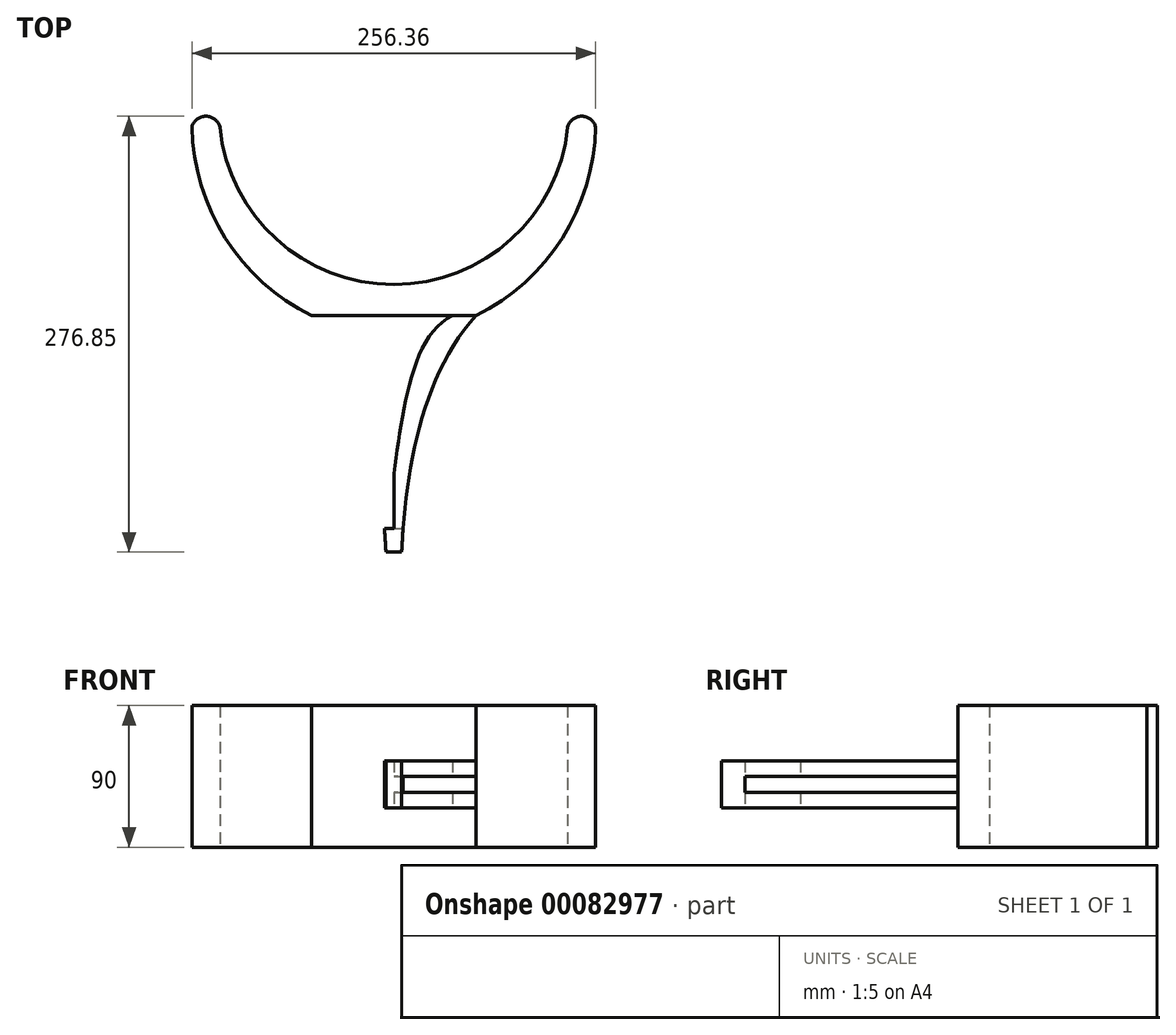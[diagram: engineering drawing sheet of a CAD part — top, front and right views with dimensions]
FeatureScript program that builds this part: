
annotation { "Feature Type Name" : "Feature", "Feature Type Description" : "" }
export const myFeature = defineFeature(function(context is Context, id is Id, definition is map)
    precondition{}
    {
        {
            var Q0;
            Q0=qCreatedBy(makeId("Top.planeOp"),FACE);
            var sketch = newSketch(context, id + "F0", { "sketchPlane" : qUnion([Q0])});
            skLineSegment(sketch, "E0", {"start": v(0, -100) * mm, "end": v(0, -119.8) * mm});
            skLineSegment(sketch, "E1.MirrorCS", {"start": v(0, -119.8) * mm, "end": v(-52.27, -119.8) * mm});
            skArc(sketch, "E2", {"start": v(-110.44, 0) * mm, "mid": v(-119.3, 6.83) * mm, "end": v(-128.18, 0) * mm});
            skArc(sketch, "E3", {"start": v(-128.18, 0) * mm, "mid": v(-107.02, -70.54) * mm, "end": v(-52.27, -119.8) * mm});
            skLineSegment(sketch, "E4", {"start": v(0, 0) * mm, "end": v(0, -100) * mm});
            skLineSegment(sketch, "E5", {"start": v(-110.44, 0) * mm, "end": v(109.56, 0) * mm});
            skLineSegment(sketch, "E6", {"start": v(-52.27, -119.8) * mm, "end": v(-37.27, -119.8) * mm});
            skLineSegment(sketch, "E7", {"start": v(0, -270.02) * mm, "end": v(0, -220.02) * mm});
            skFitSpline(sketch, "E8", {"points": [v(-37.27, -119.8) * mm, v(0, -220.02) * mm], "startDerivative": vector(81.66, -39.68) * mm, "endDerivative": vector(16.88, -110.04) * mm});
            skArc(sketch, "E9.MirrorCS", {"start": v(110.44, 0) * mm, "mid": v(119.3, 6.83) * mm, "end": v(128.18, 0) * mm});
            skLineSegment(sketch, "E10.MirrorCS", {"start": v(0, -119.8) * mm, "end": v(52.27, -119.8) * mm});
            skLineSegment(sketch, "E11", {"start": v(0, -270.02) * mm, "end": v(-5, -270.02) * mm});
            skFitSpline(sketch, "E12", {"points": [v(-52.27, -119.8) * mm, v(-5, -270.02) * mm], "startDerivative": vector(102.09, -110.63) * mm, "endDerivative": vector(7.68, -161.77) * mm});
            skArc(sketch, "E13", {"start": v(-110.44, 0) * mm, "mid": v(-74.53, -71.33) * mm, "end": v(0, -100) * mm});
            skArc(sketch, "E14.MirrorCS", {"start": v(110.44, 0) * mm, "mid": v(74.53, -71.33) * mm, "end": v(0, -100) * mm});
            skArc(sketch, "E15.MirrorCS", {"start": v(128.18, 0) * mm, "mid": v(107.02, -70.54) * mm, "end": v(52.27, -119.8) * mm});
            skLineSegment(sketch, "E16.MirrorCS", {"start": v(52.27, -119.8) * mm, "end": v(37.27, -119.8) * mm});
            skFitSpline(sketch, "E17.MirrorCS", {"points": [v(37.27, -119.8) * mm, v(0, -220.02) * mm], "startDerivative": vector(-81.66, -39.68) * mm, "endDerivative": vector(-16.88, -110.04) * mm});
            skFitSpline(sketch, "E18.MirrorCS", {"points": [v(52.27, -119.8) * mm, v(5, -270.02) * mm], "startDerivative": vector(-102.09, -110.63) * mm, "endDerivative": vector(-7.68, -161.77) * mm});
            skLineSegment(sketch, "E19.MirrorCS", {"start": v(0, -270.02) * mm, "end": v(5, -270.02) * mm});
            skLineSegment(sketch, "E20", {"start": v(-5.91, -255.15) * mm, "end": v(5.91, -255.15) * mm});
            skSolve(sketch);
        }
        {
            var Q0;
            {var subQ1=sQuery(id+"F0.wireOp",EDGE,"E6");Q0=makeQuery(id+"F0.imprint","IMPRINT",FACE,{"disambiguationData":[TD([[makeQuery(id+"F0.imprint","IMPRINT",EDGE,{"derivedFrom":subQ1}),-1.0]])]});}
            var Q1;
            {var subQ0=sQuery(id+"F0.wireOp",EDGE,"E17.MirrorCS");Q1=makeQuery(id+"F0.imprint","IMPRINT",FACE,{"disambiguationData":[TD([[makeQuery(id+"F0.imprint","IMPRINT",EDGE,{"derivedFrom":subQ0}),1.0]])]});}
            var Q2;
            {var subQ0=sQuery(id+"F0.wireOp",EDGE,"E19.MirrorCS");Q2=makeQuery(id+"F0.imprint","IMPRINT",FACE,{"disambiguationData":[TD([[makeQuery(id+"F0.imprint","IMPRINT",EDGE,{"derivedFrom":subQ0}),1.0]])]});}
            var Q3;
            {var subQ0=sQuery(id+"F0.wireOp",EDGE,"E11");Q3=makeQuery(id+"F0.imprint","IMPRINT",FACE,{"disambiguationData":[TD([[makeQuery(id+"F0.imprint","IMPRINT",EDGE,{"derivedFrom":subQ0}),-1.0]])]});}
            extrude(context, id + "F1", {"entities" : qUnion([Q0, Q1, Q2, Q3]), "depth" : 15 * mm, "hasSecondDirection" : true, "secondDirectionOppositeDirection" : true, "secondDirectionDepth" : 15 * mm});
        }
        {
            var Q0;
            Q0=makeQuery(id+"F0.imprint","IMPRINT",FACE,{"disambiguationData":[TD([[makeQuery(id+"F0.imprint","IMPRINT",EDGE,{"derivedFrom":sQuery(id+"F0.wireOp",EDGE,"E0")}),-1.0]])]});
            var Q1;
            {var subQ4=sQuery(id+"F0.wireOp",EDGE,"E0");Q1=makeQuery(id+"F0.imprint","IMPRINT",FACE,{"disambiguationData":[TD([[makeQuery(id+"F0.imprint","IMPRINT",EDGE,{"derivedFrom":subQ4}),1.0]])]});}
            extrude(context, id + "F2", {"entities" : qUnion([Q0, Q1]), "operationType" : NewBodyOperationType.ADD, "depth" : 50 * mm, "hasSecondDirection" : true, "secondDirectionOppositeDirection" : true, "secondDirectionDepth" : 40 * mm});
        }
        {
            var Q0;
            {var subQ1=sQuery(id+"F0.wireOp",EDGE,"E6");Q0=makeQuery(id+"F0.imprint","IMPRINT",FACE,{"disambiguationData":[TD([[makeQuery(id+"F0.imprint","IMPRINT",EDGE,{"derivedFrom":subQ1}),-1.0]])]});}
            var Q1;
            {var subQ0=sQuery(id+"F0.wireOp",EDGE,"E17.MirrorCS");Q1=makeQuery(id+"F0.imprint","IMPRINT",FACE,{"disambiguationData":[TD([[makeQuery(id+"F0.imprint","IMPRINT",EDGE,{"derivedFrom":subQ0}),1.0]])]});}
            extrude(context, id + "F3", {"entities" : qUnion([Q0, Q1]), "operationType" : NewBodyOperationType.REMOVE, "oppositeDirection" : true, "depth" : 5 * mm, "hasSecondDirection" : true, "secondDirectionOppositeDirection" : false, "secondDirectionDepth" : 5 * mm});
        }
    });
